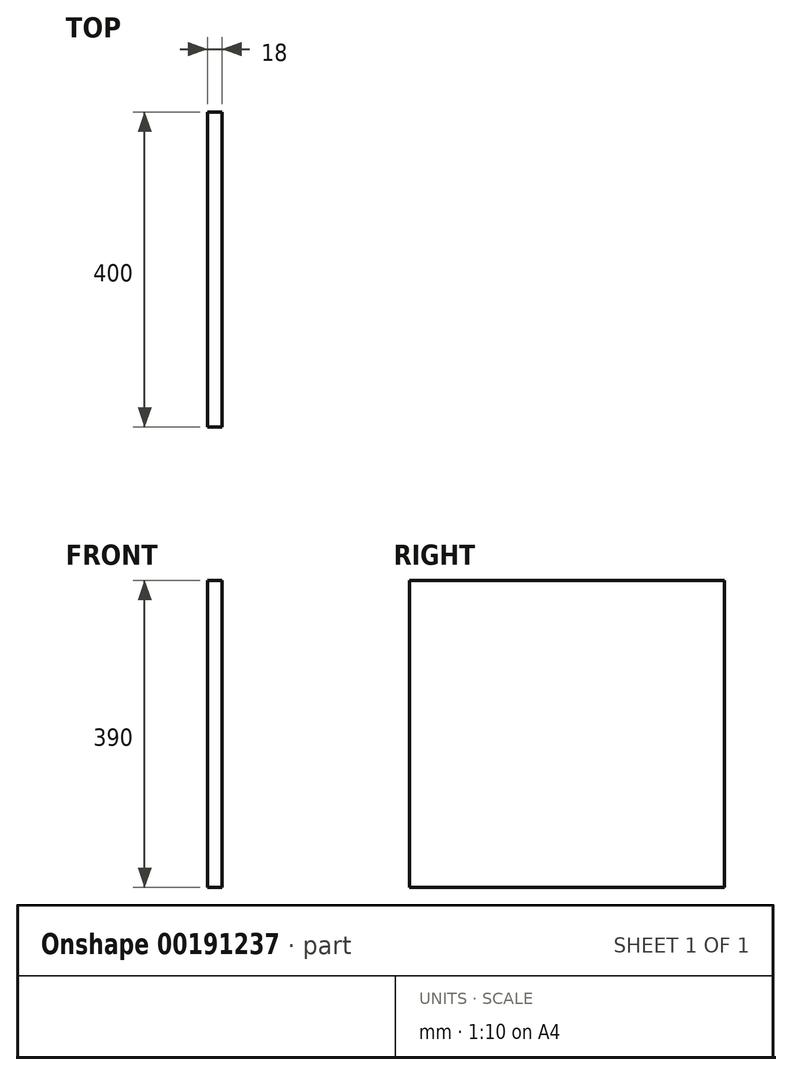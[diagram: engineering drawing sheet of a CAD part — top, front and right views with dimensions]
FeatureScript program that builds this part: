
annotation { "Feature Type Name" : "Feature", "Feature Type Description" : "" }
export const myFeature = defineFeature(function(context is Context, id is Id, definition is map)
    precondition{}
    {
        {
            var Q0;
            Q0=qCreatedBy(makeId("Right.planeOp"),FACE);
            var sketch = newSketch(context, id + "F0", { "sketchPlane" : qUnion([Q0])});
            skLineSegment(sketch, "E0.bottom", {"start": v(0, 0) * mm, "end": v(-400, 0) * mm});
            skLineSegment(sketch, "E0.top", {"start": v(0, 390) * mm, "end": v(-400, 390) * mm});
            skLineSegment(sketch, "E0.left", {"start": v(0, 0) * mm, "end": v(0, 390) * mm});
            skLineSegment(sketch, "E0.right", {"start": v(-400, 0) * mm, "end": v(-400, 390) * mm});
            skSolve(sketch);
        }
        {
            var Q0;
            Q0 = qSketchRegion(id + "F0", true);
            extrude(context, id + "F1", {"entities" : qUnion([Q0]), "depth" : 18 * mm});
        }
    });
